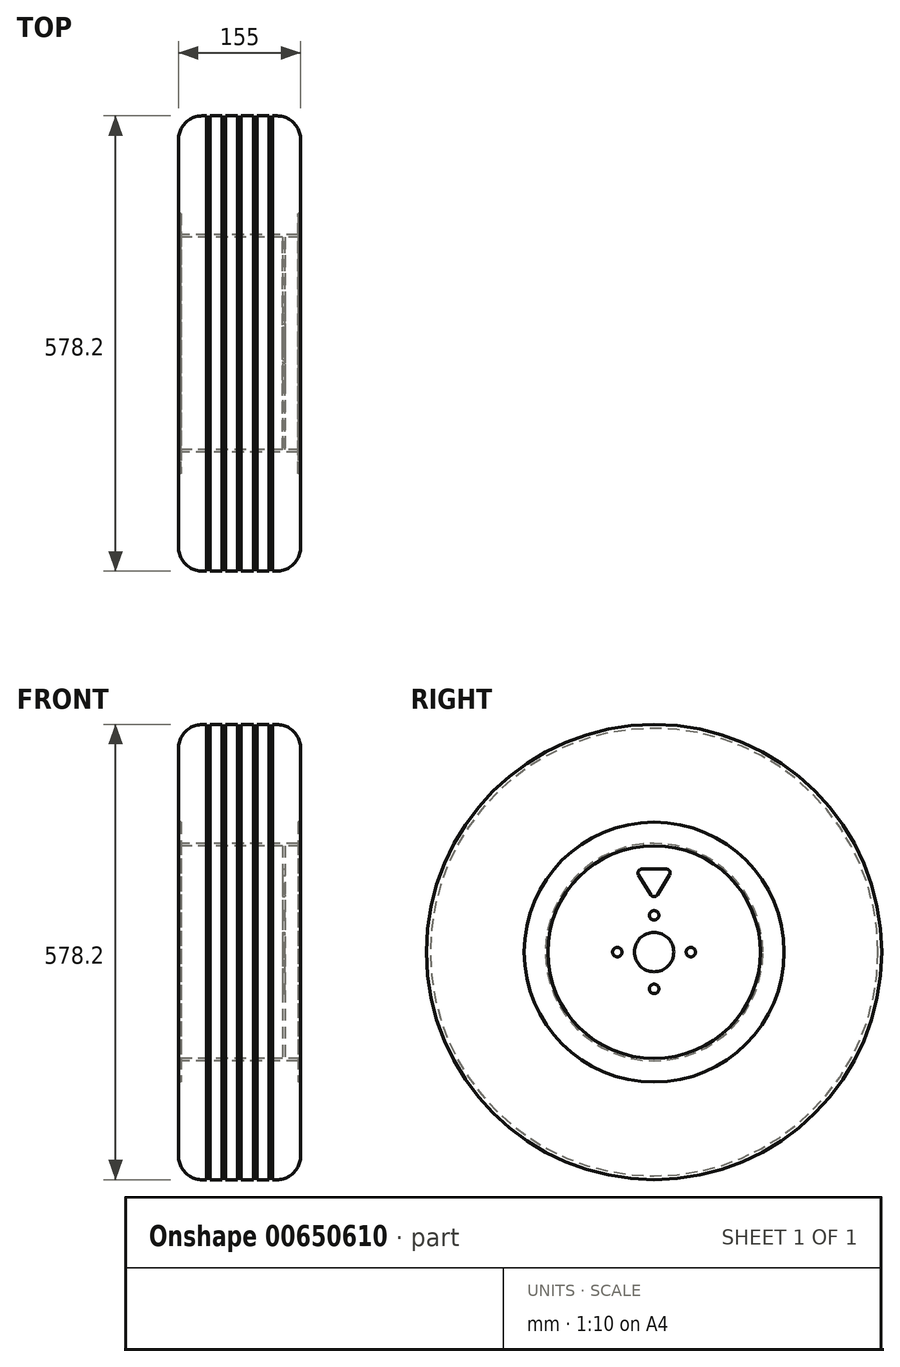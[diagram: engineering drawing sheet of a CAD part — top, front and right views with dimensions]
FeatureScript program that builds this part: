
annotation { "Feature Type Name" : "Feature", "Feature Type Description" : "" }
export const myFeature = defineFeature(function(context is Context, id is Id, definition is map)
    precondition{}
    {
        {
            var Q0;
            Q0=qCreatedBy(makeId("Top.planeOp"),FACE);
            var sketch = newSketch(context, id + "F0", { "sketchPlane" : qUnion([Q0])});
            skLineSegment(sketch, "E0", {"start": v(-135, 165.1) * mm, "end": v(-135, 135.1) * mm});
            skLineSegment(sketch, "E1", {"start": v(-135, 135.1) * mm, "end": v(20, 135.1) * mm});
            skLineSegment(sketch, "E2", {"start": v(20, 135.1) * mm, "end": v(20, 165.1) * mm});
            skLineSegment(sketch, "E3.0", {"start": v(17, 138.1) * mm, "end": v(17, 165.1) * mm});
            skLineSegment(sketch, "E3.1", {"start": v(-132, 138.1) * mm, "end": v(17, 138.1) * mm});
            skLineSegment(sketch, "E3.2", {"start": v(-132, 165.1) * mm, "end": v(-132, 138.1) * mm});
            skLineSegment(sketch, "E4", {"start": v(-133, 165.1) * mm, "end": v(-132, 165.1) * mm});
            skLineSegment(sketch, "E5", {"start": v(17, 165.1) * mm, "end": v(18, 165.1) * mm});
            skLineSegment(sketch, "E6", {"start": v(0, 135.1) * mm, "end": v(0, 0) * mm});
            skLineSegment(sketch, "E7", {"start": v(0, 0) * mm, "end": v(-3, 0) * mm});
            skLineSegment(sketch, "E8", {"start": v(-3, 0) * mm, "end": v(-3, 135.1) * mm});
            skLineSegment(sketch, "E9", {"start": v(-17.96, 0) * mm, "end": v(21.43, 0) * mm, "construction": true});
            skLineSegment(sketch, "E10", {"start": v(20, 167.1) * mm, "end": v(20, 259.1) * mm});
            skLineSegment(sketch, "E11", {"start": v(-10, 289.1) * mm, "end": v(-15.73, 289.1) * mm});
            skLineSegment(sketch, "E12", {"start": v(-135, 259.1) * mm, "end": v(-135, 167.1) * mm});
            skPoint(sketch, "E13.visualSharp", {"position": v(-135, 289.1) * mm});
            skArc(sketch, "E13.filletArc", {"start": v(-105, 289.1) * mm, "mid": v(-126.21, 280.31) * mm, "end": v(-135, 259.1) * mm});
            skPoint(sketch, "E14.visualSharp", {"position": v(20, 289.1) * mm});
            skArc(sketch, "E14.filletArc", {"start": v(20, 259.1) * mm, "mid": v(11.21, 280.31) * mm, "end": v(-10, 289.1) * mm});
            skPoint(sketch, "E15.visualSharp", {"position": v(-135, 165.1) * mm});
            skArc(sketch, "E15.filletArc", {"start": v(-135, 167.1) * mm, "mid": v(-134.41, 165.69) * mm, "end": v(-133, 165.1) * mm});
            skPoint(sketch, "E16.visualSharp", {"position": v(20, 165.1) * mm});
            skArc(sketch, "E16.filletArc", {"start": v(18, 165.1) * mm, "mid": v(19.41, 165.69) * mm, "end": v(20, 167.1) * mm});
            skLineSegment(sketch, "E17", {"start": v(20, 165.1) * mm, "end": v(18, 165.1) * mm});
            skLineSegment(sketch, "E18", {"start": v(-133, 165.1) * mm, "end": v(-135, 165.1) * mm});
            skLineSegment(sketch, "E19.top", {"start": v(-99.27, 284.33) * mm, "end": v(-94.83, 284.33) * mm});
            skLineSegment(sketch, "E19.left", {"start": v(-99.27, 289.1) * mm, "end": v(-99.27, 284.33) * mm});
            skLineSegment(sketch, "E19.right", {"start": v(-94.83, 289.1) * mm, "end": v(-94.83, 284.33) * mm});
            skLineSegment(sketch, "E20.top", {"start": v(-79.5, 284.33) * mm, "end": v(-75.06, 284.33) * mm});
            skLineSegment(sketch, "E20.left", {"start": v(-79.5, 289.1) * mm, "end": v(-79.5, 284.33) * mm});
            skLineSegment(sketch, "E20.right", {"start": v(-75.06, 289.1) * mm, "end": v(-75.06, 284.33) * mm});
            skLineSegment(sketch, "E21.top", {"start": v(-59.72, 284.33) * mm, "end": v(-55.28, 284.33) * mm});
            skLineSegment(sketch, "E21.left", {"start": v(-59.72, 289.1) * mm, "end": v(-59.72, 284.33) * mm});
            skLineSegment(sketch, "E21.right", {"start": v(-55.28, 289.1) * mm, "end": v(-55.28, 284.33) * mm});
            skLineSegment(sketch, "E22.top", {"start": v(-39.94, 284.33) * mm, "end": v(-35.5, 284.33) * mm});
            skLineSegment(sketch, "E22.left", {"start": v(-39.94, 289.1) * mm, "end": v(-39.94, 284.33) * mm});
            skLineSegment(sketch, "E22.right", {"start": v(-35.5, 289.1) * mm, "end": v(-35.5, 284.33) * mm});
            skLineSegment(sketch, "E23.top", {"start": v(-20.17, 284.33) * mm, "end": v(-15.73, 284.33) * mm});
            skLineSegment(sketch, "E23.left", {"start": v(-20.17, 289.1) * mm, "end": v(-20.17, 284.33) * mm});
            skLineSegment(sketch, "E23.right", {"start": v(-15.73, 289.1) * mm, "end": v(-15.73, 284.33) * mm});
            skLineSegment(sketch, "E24.trimOffspring", {"start": v(-99.27, 289.1) * mm, "end": v(-105, 289.1) * mm});
            skLineSegment(sketch, "E25.trimOffspring", {"start": v(-79.5, 289.1) * mm, "end": v(-94.83, 289.1) * mm});
            skLineSegment(sketch, "E26.trimOffspring", {"start": v(-59.72, 289.1) * mm, "end": v(-75.06, 289.1) * mm});
            skLineSegment(sketch, "E27.trimOffspring", {"start": v(-39.94, 289.1) * mm, "end": v(-55.28, 289.1) * mm});
            skLineSegment(sketch, "E28.trimOffspring", {"start": v(-20.17, 289.1) * mm, "end": v(-35.5, 289.1) * mm});
            skSolve(sketch);
        }
        {
            var Q0;
            {var subQ4=sQuery(id+"F0.wireOp",EDGE,"E0");Q0=makeQuery(id+"F0.imprint","IMPRINT",FACE,{"disambiguationData":[TD([[makeQuery(id+"F0.imprint","IMPRINT",EDGE,{"derivedFrom":subQ4}),1.0]])]});}
            var Q1;
            {var subQ0=sQuery(id+"F0.wireOp",EDGE,"E6");Q1=makeQuery(id+"F0.imprint","IMPRINT",FACE,{"disambiguationData":[TD([[makeQuery(id+"F0.imprint","IMPRINT",EDGE,{"derivedFrom":subQ0}),-1.0]])]});}
            var Q2;
            Q2=sQuery(id+"F0.wireOp",EDGE,"E9");
            revolve(context, id + "F1", {"entities" : qUnion([Q0, Q1]), "axis" : qUnion([Q2]), "revolveType" : RevolveType.FULL});
        }
        {
            var Q0;
            Q0=makeQuery(id+"F1.opRevolve","SWEPT_FACE",FACE,{"disambiguationData":[OSD([sQuery(id+"F0.wireOp",EDGE,"E6")])]});
            var sketch = newSketch(context, id + "F2", { "sketchPlane" : qUnion([Q0])});
            skCircle(sketch, "E29", {"center": v(0, 0) * mm, "radius": 25 * mm});
            skCircle(sketch, "E30", {"center": v(0, 46.7) * mm, "radius": 6 * mm});
            skCircle(sketch, "E31.1.0", {"center": v(-46.7, 0) * mm, "radius": 6 * mm});
            skCircle(sketch, "E31.2.0", {"center": v(0, -46.7) * mm, "radius": 6 * mm});
            skCircle(sketch, "E31.3.0", {"center": v(46.7, 0) * mm, "radius": 6 * mm});
            skLineSegment(sketch, "E32", {"start": v(4.25, 72.84) * mm, "end": v(19.73, 97.84) * mm});
            skLineSegment(sketch, "E33", {"start": v(15.48, 105.48) * mm, "end": v(0, 105.48) * mm});
            skPoint(sketch, "E34.visualSharp", {"position": v(24.45, 105.48) * mm});
            skArc(sketch, "E34.filletArc", {"start": v(19.73, 97.84) * mm, "mid": v(19.84, 102.9) * mm, "end": v(15.48, 105.48) * mm});
            skLineSegment(sketch, "E35.MirrorCS", {"start": v(-15.48, 105.48) * mm, "end": v(0, 105.48) * mm});
            skArc(sketch, "E36.MirrorCS", {"start": v(-19.73, 97.84) * mm, "mid": v(-19.84, 102.9) * mm, "end": v(-15.48, 105.48) * mm});
            skLineSegment(sketch, "E37.MirrorCS", {"start": v(-4.25, 72.84) * mm, "end": v(-19.73, 97.84) * mm});
            skPoint(sketch, "E38.visualSharp", {"position": v(0, 65.97) * mm});
            skArc(sketch, "E38.filletArc", {"start": v(-4.25, 72.84) * mm, "mid": v(0, 70.47) * mm, "end": v(4.25, 72.84) * mm});
            skArc(sketch, "E39.1.0", {"start": v(-83.14, 55.24) * mm, "mid": v(-86.8, 58.74) * mm, "end": v(-85.53, 63.64) * mm});
            skLineSegment(sketch, "E39.1.1", {"start": v(-54.51, 48.5) * mm, "end": v(-83.14, 55.24) * mm});
            skLineSegment(sketch, "E39.1.2", {"start": v(-85.53, 63.64) * mm, "end": v(-74.58, 74.58) * mm});
            skLineSegment(sketch, "E39.1.3", {"start": v(-48.5, 54.51) * mm, "end": v(-55.24, 83.14) * mm});
            skLineSegment(sketch, "E39.1.4", {"start": v(-63.64, 85.53) * mm, "end": v(-74.58, 74.58) * mm});
            skPoint(sketch, "E39.1.5", {"position": v(-57.3, 91.87) * mm});
            skArc(sketch, "E39.1.6", {"start": v(-55.24, 83.14) * mm, "mid": v(-58.74, 86.8) * mm, "end": v(-63.64, 85.53) * mm});
            skPoint(sketch, "E39.1.7", {"position": v(-46.65, 46.65) * mm});
            skArc(sketch, "E39.1.8", {"start": v(-54.51, 48.5) * mm, "mid": v(-49.83, 49.83) * mm, "end": v(-48.5, 54.51) * mm});
            skArc(sketch, "E39.2.0", {"start": v(-97.84, -19.73) * mm, "mid": v(-102.9, -19.84) * mm, "end": v(-105.48, -15.48) * mm});
            skLineSegment(sketch, "E39.2.1", {"start": v(-72.84, -4.25) * mm, "end": v(-97.84, -19.73) * mm});
            skLineSegment(sketch, "E39.2.2", {"start": v(-105.48, -15.48) * mm, "end": v(-105.48, 0) * mm});
            skLineSegment(sketch, "E39.2.3", {"start": v(-72.84, 4.25) * mm, "end": v(-97.84, 19.73) * mm});
            skLineSegment(sketch, "E39.2.4", {"start": v(-105.48, 15.48) * mm, "end": v(-105.48, 0) * mm});
            skPoint(sketch, "E39.2.5", {"position": v(-105.48, 24.45) * mm});
            skArc(sketch, "E39.2.6", {"start": v(-97.84, 19.73) * mm, "mid": v(-102.9, 19.84) * mm, "end": v(-105.48, 15.48) * mm});
            skPoint(sketch, "E39.2.7", {"position": v(-65.97, 0) * mm});
            skArc(sketch, "E39.2.8", {"start": v(-72.84, -4.25) * mm, "mid": v(-70.47, 0) * mm, "end": v(-72.84, 4.25) * mm});
            skArc(sketch, "E39.3.0", {"start": v(-55.24, -83.14) * mm, "mid": v(-58.74, -86.8) * mm, "end": v(-63.64, -85.53) * mm});
            skLineSegment(sketch, "E39.3.1", {"start": v(-48.5, -54.51) * mm, "end": v(-55.24, -83.14) * mm});
            skLineSegment(sketch, "E39.3.2", {"start": v(-63.64, -85.53) * mm, "end": v(-74.58, -74.58) * mm});
            skLineSegment(sketch, "E39.3.3", {"start": v(-54.51, -48.5) * mm, "end": v(-83.14, -55.24) * mm});
            skLineSegment(sketch, "E39.3.4", {"start": v(-85.53, -63.64) * mm, "end": v(-74.58, -74.58) * mm});
            skPoint(sketch, "E39.3.5", {"position": v(-91.87, -57.3) * mm});
            skArc(sketch, "E39.3.6", {"start": v(-83.14, -55.24) * mm, "mid": v(-86.8, -58.74) * mm, "end": v(-85.53, -63.64) * mm});
            skPoint(sketch, "E39.3.7", {"position": v(-46.65, -46.65) * mm});
            skArc(sketch, "E39.3.8", {"start": v(-48.5, -54.51) * mm, "mid": v(-49.83, -49.83) * mm, "end": v(-54.51, -48.5) * mm});
            skArc(sketch, "E39.4.0", {"start": v(19.73, -97.84) * mm, "mid": v(19.84, -102.9) * mm, "end": v(15.48, -105.48) * mm});
            skLineSegment(sketch, "E39.4.1", {"start": v(4.25, -72.84) * mm, "end": v(19.73, -97.84) * mm});
            skLineSegment(sketch, "E39.4.2", {"start": v(15.48, -105.48) * mm, "end": v(0, -105.48) * mm});
            skLineSegment(sketch, "E39.4.3", {"start": v(-4.25, -72.84) * mm, "end": v(-19.73, -97.84) * mm});
            skLineSegment(sketch, "E39.4.4", {"start": v(-15.48, -105.48) * mm, "end": v(0, -105.48) * mm});
            skPoint(sketch, "E39.4.5", {"position": v(-24.45, -105.48) * mm});
            skArc(sketch, "E39.4.6", {"start": v(-19.73, -97.84) * mm, "mid": v(-19.84, -102.9) * mm, "end": v(-15.48, -105.48) * mm});
            skPoint(sketch, "E39.4.7", {"position": v(0, -65.97) * mm});
            skArc(sketch, "E39.4.8", {"start": v(4.25, -72.84) * mm, "mid": v(0, -70.47) * mm, "end": v(-4.25, -72.84) * mm});
            skArc(sketch, "E39.5.0", {"start": v(83.14, -55.24) * mm, "mid": v(86.8, -58.74) * mm, "end": v(85.53, -63.64) * mm});
            skLineSegment(sketch, "E39.5.1", {"start": v(54.51, -48.5) * mm, "end": v(83.14, -55.24) * mm});
            skLineSegment(sketch, "E39.5.2", {"start": v(85.53, -63.64) * mm, "end": v(74.58, -74.58) * mm});
            skLineSegment(sketch, "E39.5.3", {"start": v(48.5, -54.51) * mm, "end": v(55.24, -83.14) * mm});
            skLineSegment(sketch, "E39.5.4", {"start": v(63.64, -85.53) * mm, "end": v(74.58, -74.58) * mm});
            skPoint(sketch, "E39.5.5", {"position": v(57.3, -91.87) * mm});
            skArc(sketch, "E39.5.6", {"start": v(55.24, -83.14) * mm, "mid": v(58.74, -86.8) * mm, "end": v(63.64, -85.53) * mm});
            skPoint(sketch, "E39.5.7", {"position": v(46.65, -46.65) * mm});
            skArc(sketch, "E39.5.8", {"start": v(54.51, -48.5) * mm, "mid": v(49.83, -49.83) * mm, "end": v(48.5, -54.51) * mm});
            skArc(sketch, "E39.6.0", {"start": v(97.84, 19.73) * mm, "mid": v(102.9, 19.84) * mm, "end": v(105.48, 15.48) * mm});
            skLineSegment(sketch, "E39.6.1", {"start": v(72.84, 4.25) * mm, "end": v(97.84, 19.73) * mm});
            skLineSegment(sketch, "E39.6.2", {"start": v(105.48, 15.48) * mm, "end": v(105.48, 0) * mm});
            skLineSegment(sketch, "E39.6.3", {"start": v(72.84, -4.25) * mm, "end": v(97.84, -19.73) * mm});
            skLineSegment(sketch, "E39.6.4", {"start": v(105.48, -15.48) * mm, "end": v(105.48, 0) * mm});
            skPoint(sketch, "E39.6.5", {"position": v(105.48, -24.45) * mm});
            skArc(sketch, "E39.6.6", {"start": v(97.84, -19.73) * mm, "mid": v(102.9, -19.84) * mm, "end": v(105.48, -15.48) * mm});
            skPoint(sketch, "E39.6.7", {"position": v(65.97, 0) * mm});
            skArc(sketch, "E39.6.8", {"start": v(72.84, 4.25) * mm, "mid": v(70.47, 0) * mm, "end": v(72.84, -4.25) * mm});
            skArc(sketch, "E39.7.0", {"start": v(55.24, 83.14) * mm, "mid": v(58.74, 86.8) * mm, "end": v(63.64, 85.53) * mm});
            skLineSegment(sketch, "E39.7.1", {"start": v(48.5, 54.51) * mm, "end": v(55.24, 83.14) * mm});
            skLineSegment(sketch, "E39.7.2", {"start": v(63.64, 85.53) * mm, "end": v(74.58, 74.58) * mm});
            skLineSegment(sketch, "E39.7.3", {"start": v(54.51, 48.5) * mm, "end": v(83.14, 55.24) * mm});
            skLineSegment(sketch, "E39.7.4", {"start": v(85.53, 63.64) * mm, "end": v(74.58, 74.58) * mm});
            skPoint(sketch, "E39.7.5", {"position": v(91.87, 57.3) * mm});
            skArc(sketch, "E39.7.6", {"start": v(83.14, 55.24) * mm, "mid": v(86.8, 58.74) * mm, "end": v(85.53, 63.64) * mm});
            skPoint(sketch, "E39.7.7", {"position": v(46.65, 46.65) * mm});
            skArc(sketch, "E39.7.8", {"start": v(48.5, 54.51) * mm, "mid": v(49.83, 49.83) * mm, "end": v(54.51, 48.5) * mm});
            skSolve(sketch);
        }
        {
            var Q0;
            Q0=makeQuery(id+"F2.imprint","IMPRINT",FACE,{"disambiguationData":[TD([[makeQuery(id+"F2.imprint","IMPRINT",EDGE,{"derivedFrom":sQuery(id+"F2.wireOp",EDGE,"E29")}),1.0]])]});
            var Q1;
            Q1=makeQuery(id+"F2.imprint","IMPRINT",FACE,{"disambiguationData":[TD([[makeQuery(id+"F2.imprint","IMPRINT",EDGE,{"derivedFrom":sQuery(id+"F2.wireOp",EDGE,"E31.1.0")}),1.0]])]});
            var Q2;
            Q2=makeQuery(id+"F2.imprint","IMPRINT",FACE,{"disambiguationData":[TD([[makeQuery(id+"F2.imprint","IMPRINT",EDGE,{"derivedFrom":sQuery(id+"F2.wireOp",EDGE,"E30")}),1.0]])]});
            var Q3;
            Q3=makeQuery(id+"F2.imprint","IMPRINT",FACE,{"disambiguationData":[TD([[makeQuery(id+"F2.imprint","IMPRINT",EDGE,{"derivedFrom":sQuery(id+"F2.wireOp",EDGE,"E31.3.0")}),1.0]])]});
            var Q4;
            Q4=makeQuery(id+"F2.imprint","IMPRINT",FACE,{"disambiguationData":[TD([[makeQuery(id+"F2.imprint","IMPRINT",EDGE,{"derivedFrom":sQuery(id+"F2.wireOp",EDGE,"E31.2.0")}),1.0]])]});
            var Q5;
            Q5=makeQuery(id+"F2.imprint","IMPRINT",FACE,{"disambiguationData":[TD([[makeQuery(id+"F2.imprint","IMPRINT",EDGE,{"derivedFrom":sQuery(id+"F2.wireOp",EDGE,"E32")}),1.0]])]});
            var Q6;
            Q6=makeQuery(id+"F2.imprint","IMPRINT",FACE,{"disambiguationData":[TD([[makeQuery(id+"F2.imprint","IMPRINT",EDGE,{"derivedFrom":sQuery(id+"F2.wireOp",EDGE,"E39.7.0")}),-1.0]])]});
            var Q7;
            Q7=makeQuery(id+"F2.imprint","IMPRINT",FACE,{"disambiguationData":[TD([[makeQuery(id+"F2.imprint","IMPRINT",EDGE,{"derivedFrom":sQuery(id+"F2.wireOp",EDGE,"E39.6.0")}),-1.0]])]});
            var Q8;
            Q8=makeQuery(id+"F2.imprint","IMPRINT",FACE,{"disambiguationData":[TD([[makeQuery(id+"F2.imprint","IMPRINT",EDGE,{"derivedFrom":sQuery(id+"F2.wireOp",EDGE,"E39.4.0")}),-1.0]])]});
            var Q9;
            Q9=makeQuery(id+"F2.imprint","IMPRINT",FACE,{"disambiguationData":[TD([[makeQuery(id+"F2.imprint","IMPRINT",EDGE,{"derivedFrom":sQuery(id+"F2.wireOp",EDGE,"E39.3.0")}),-1.0]])]});
            var Q10;
            Q10=makeQuery(id+"F2.imprint","IMPRINT",FACE,{"disambiguationData":[TD([[makeQuery(id+"F2.imprint","IMPRINT",EDGE,{"derivedFrom":sQuery(id+"F2.wireOp",EDGE,"E39.2.0")}),-1.0]])]});
            var Q11;
            Q11=makeQuery(id+"F2.imprint","IMPRINT",FACE,{"disambiguationData":[TD([[makeQuery(id+"F2.imprint","IMPRINT",EDGE,{"derivedFrom":sQuery(id+"F2.wireOp",EDGE,"E39.1.0")}),-1.0]])]});
            var Q12;
            Q12=makeQuery(id+"F2.imprint","IMPRINT",FACE,{"disambiguationData":[TD([[makeQuery(id+"F2.imprint","IMPRINT",EDGE,{"derivedFrom":sQuery(id+"F2.wireOp",EDGE,"E39.5.0")}),-1.0]])]});
            var Q13;
            Q13=sQuery(id+"F2.wireOp",EDGE,"E30");
            var Q14;
            Q14=sQuery(id+"F2.wireOp",EDGE,"E31.1.0");
            var Q15;
            Q15=sQuery(id+"F2.wireOp",EDGE,"E29");
            var Q16;
            Q16=sQuery(id+"F2.wireOp",EDGE,"E31.3.0");
            var Q17;
            Q17=sQuery(id+"F2.wireOp",EDGE,"E31.2.0");
            extrude(context, id + "F3", {"entities" : qUnion([Q0, Q1, Q2, Q3, Q4, Q5, Q6, Q7, Q8, Q9, Q10, Q11, Q12]), "operationType" : NewBodyOperationType.REMOVE, "surfaceEntities" : qUnion([Q13, Q14, Q15, Q16, Q17]), "endBound" : BoundingType.THROUGH_ALL, "oppositeDirection" : true, "depth" : 25 * mm, "offsetDistance" : 25 * mm});
        }
        {
            var Q0;
            Q0=makeQuery(id+"F0.imprint","IMPRINT",FACE,{"disambiguationData":[TD([[makeQuery(id+"F0.imprint","IMPRINT",EDGE,{"derivedFrom":sQuery(id+"F0.wireOp",EDGE,"E3.0")}),1.0]])]});
            var Q1;
            Q1=sQuery(id+"F0.wireOp",EDGE,"E9");
            revolve(context, id + "F4", {"entities" : qUnion([Q0]), "axis" : qUnion([Q1]), "revolveType" : RevolveType.FULL});
        }
    });
